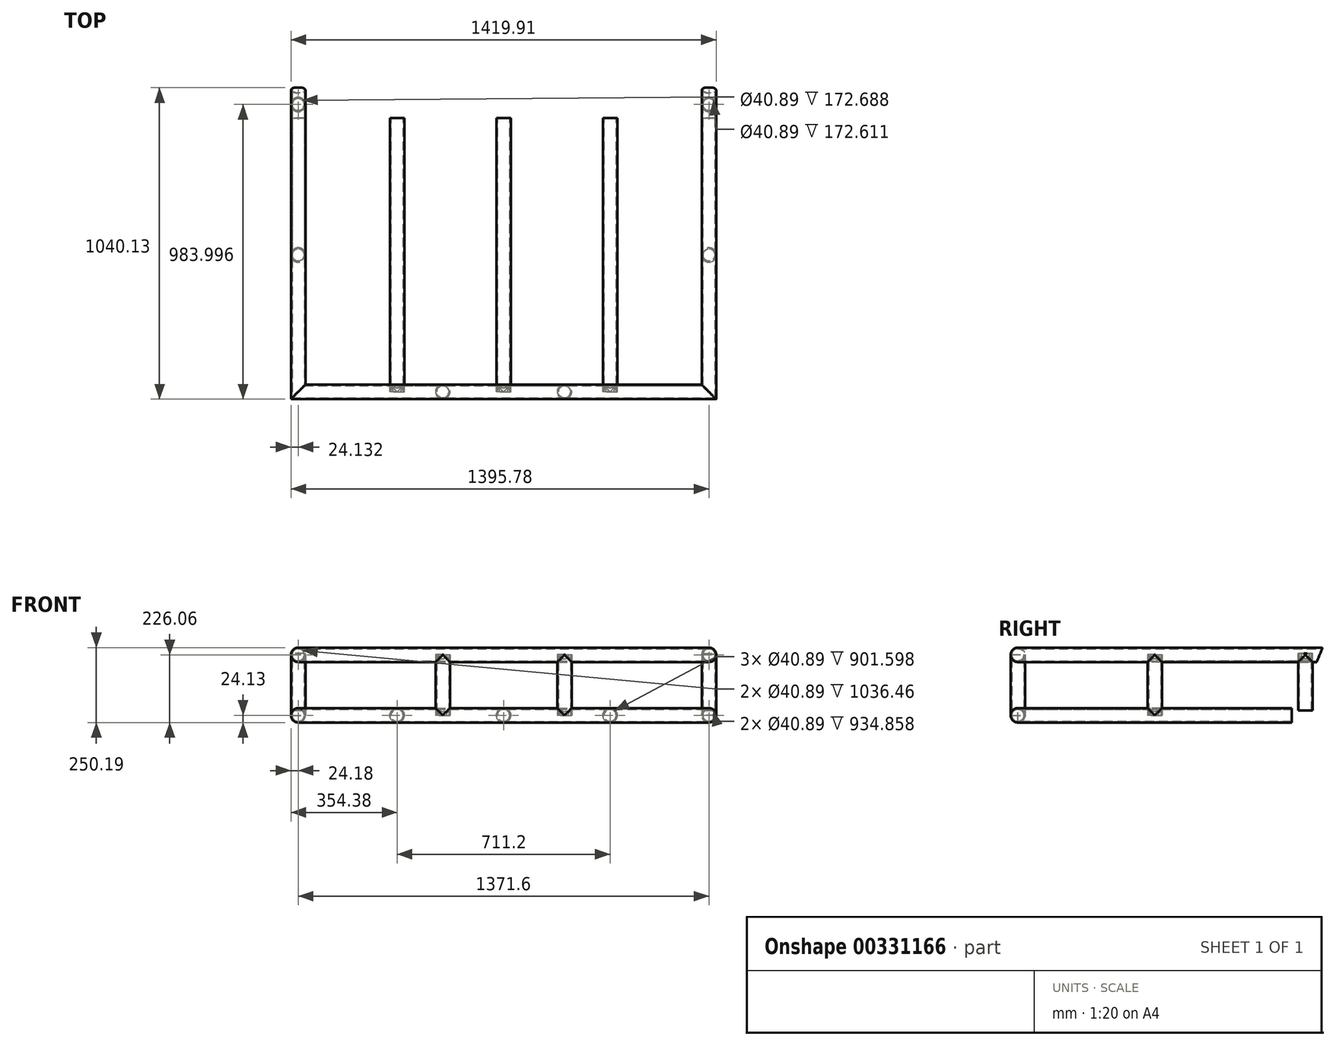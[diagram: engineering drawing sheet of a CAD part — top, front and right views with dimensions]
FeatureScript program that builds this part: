
annotation { "Feature Type Name" : "Feature", "Feature Type Description" : "" }
export const myFeature = defineFeature(function(context is Context, id is Id, definition is map)
    precondition{}
    {
        {
            var Q0;
            Q0=qCreatedBy(makeId("Front.planeOp"),FACE);
            var sketch = newSketch(context, id + "F0", { "sketchPlane" : qUnion([Q0])});
            skCircle(sketch, "E0", {"center": v(-685.8, 0) * mm, "radius": 24.13 * mm});
            skCircle(sketch, "E1", {"center": v(685.8, 0) * mm, "radius": 24.13 * mm});
            skCircle(sketch, "E2", {"center": v(685.8, 0) * mm, "radius": 20.45 * mm});
            skCircle(sketch, "E3", {"center": v(-685.8, 0) * mm, "radius": 20.45 * mm});
            skSolve(sketch);
        }
        {
            var Q0;
            Q0=qCreatedBy(makeId("Top.planeOp"),FACE);
            var sketch = newSketch(context, id + "F1", { "sketchPlane" : qUnion([Q0])});
            skLineSegment(sketch, "E4", {"start": v(-685.8, 0) * mm, "end": v(-685.8, -1016) * mm});
            skLineSegment(sketch, "E5", {"start": v(685.8, 0) * mm, "end": v(685.8, -1016) * mm});
            skLineSegment(sketch, "E6", {"start": v(-685.8, -1016) * mm, "end": v(685.8, -1016) * mm});
            skPoint(sketch, "E7.visualSharp", {"position": v(-685.8, -1016) * mm});
            skLineSegment(sketch, "E7.filletArc", {"start": v(-685.8, -1016) * mm, "end": v(-685.8, -1016) * mm});
            skPoint(sketch, "E8.visualSharp", {"position": v(685.8, -1016) * mm});
            skLineSegment(sketch, "E8.filletArc", {"start": v(685.8, -1016) * mm, "end": v(685.8, -1016) * mm});
            skLineSegment(sketch, "E9", {"start": v(-355.6, -1016) * mm, "end": v(-355.6, 0) * mm});
            skLineSegment(sketch, "E10", {"start": v(355.6, -1016) * mm, "end": v(355.6, 0) * mm});
            skLineSegment(sketch, "E11", {"start": v(0, -1016) * mm, "end": v(0, 0) * mm});
            skPoint(sketch, "E12", {"position": v(-685.8, -914.4) * mm});
            skPoint(sketch, "E13", {"position": v(685.8, -914.4) * mm});
            skPoint(sketch, "E14", {"position": v(-685.8, 0) * mm});
            skPoint(sketch, "E15", {"position": v(685.8, 0) * mm});
            skPoint(sketch, "E16", {"position": v(-355.6, -1016) * mm});
            skPoint(sketch, "E17", {"position": v(355.6, -1016) * mm});
            skSolve(sketch);
        }
        {
            var Q0;
            Q0=qCreatedBy(makeId("Front.planeOp"),FACE);
            var sketch = newSketch(context, id + "F2", { "sketchPlane" : qUnion([Q0])});
            skCircle(sketch, "E18", {"center": v(-355.6, 0) * mm, "radius": 24.13 * mm});
            skCircle(sketch, "E19", {"center": v(0, 0) * mm, "radius": 24.13 * mm});
            skCircle(sketch, "E20", {"center": v(355.6, 0) * mm, "radius": 24.13 * mm});
            skCircle(sketch, "E21", {"center": v(355.6, 0) * mm, "radius": 20.45 * mm});
            skCircle(sketch, "E22", {"center": v(0, 0) * mm, "radius": 20.45 * mm});
            skCircle(sketch, "E23", {"center": v(-355.6, 0) * mm, "radius": 20.45 * mm});
            skSolve(sketch);
        }
        {
            var Q0;
            Q0=makeQuery(id+"F0.imprint","IMPRINT",FACE,{"disambiguationData":[TD([[makeQuery(id+"F0.imprint","IMPRINT",EDGE,{"derivedFrom":sQuery(id+"F0.wireOp",EDGE,"E0")}),1.0]])]});
            var Q1;
            Q1=sQuery(id+"F1.wireOp",EDGE,"E4");
            var Q2;
            Q2=sQuery(id+"F1.wireOp",EDGE,"E7.filletArc");
            var Q3;
            Q3=sQuery(id+"F1.wireOp",EDGE,"E6");
            var Q4;
            Q4=sQuery(id+"F1.wireOp",EDGE,"E8.filletArc");
            var Q5;
            Q5=sQuery(id+"F1.wireOp",EDGE,"E5");
            sweep(context, id + "F3", {"profiles" : qUnion([Q0]), "path" : qUnion([Q1, Q2, Q3, Q4, Q5])});
        }
        {
            var Q0;
            Q0=makeQuery(id+"F2.imprint","IMPRINT",FACE,{"disambiguationData":[TD([[makeQuery(id+"F2.imprint","IMPRINT",EDGE,{"derivedFrom":sQuery(id+"F2.wireOp",EDGE,"E18")}),1.0]])]});
            var Q1;
            Q1=makeQuery(id+"F2.imprint","IMPRINT",FACE,{"disambiguationData":[TD([[makeQuery(id+"F2.imprint","IMPRINT",EDGE,{"derivedFrom":sQuery(id+"F2.wireOp",EDGE,"E19")}),1.0]])]});
            var Q2;
            Q2=makeQuery(id+"F2.imprint","IMPRINT",FACE,{"disambiguationData":[TD([[makeQuery(id+"F2.imprint","IMPRINT",EDGE,{"derivedFrom":sQuery(id+"F2.wireOp",EDGE,"E20")}),1.0]])]});
            extrude(context, id + "F4", {"entities" : qUnion([Q0, Q1, Q2]), "operationType" : NewBodyOperationType.ADD, "depth" : 1016 * mm});
        }
        {
            var Q0;
            Q0=qCreatedBy(makeId("Top.planeOp"),FACE);
            var sketch = newSketch(context, id + "F5", { "sketchPlane" : qUnion([Q0])});
            skCircle(sketch, "E24", {"center": v(-685.8, -558.8) * mm, "radius": 24.13 * mm});
            skCircle(sketch, "E25", {"center": v(685.8, -558.8) * mm, "radius": 24.13 * mm});
            skCircle(sketch, "E26", {"center": v(-203.2, -1016) * mm, "radius": 24.13 * mm});
            skCircle(sketch, "E27", {"center": v(203.2, -1016) * mm, "radius": 24.13 * mm});
            skCircle(sketch, "E28", {"center": v(-685.8, -558.8) * mm, "radius": 20.45 * mm});
            skCircle(sketch, "E29", {"center": v(685.8, -558.8) * mm, "radius": 20.45 * mm});
            skCircle(sketch, "E30", {"center": v(-203.2, -1016) * mm, "radius": 20.45 * mm});
            skCircle(sketch, "E31", {"center": v(203.2, -1016) * mm, "radius": 20.45 * mm});
            skSolve(sketch);
        }
        {
            var Q0;
            Q0 = qSketchRegion(id + "F5", true);
            extrude(context, id + "F6", {"entities" : qUnion([Q0]), "operationType" : NewBodyOperationType.ADD, "depth" : 203.2 * mm});
        }
        {
            var Q0;
            Q0=qCreatedBy(makeId("Front.planeOp"),FACE);
            var sketch = newSketch(context, id + "F7", { "sketchPlane" : qUnion([Q0])});
            skCircle(sketch, "E32", {"center": v(685.8, 201.93) * mm, "radius": 24.13 * mm});
            skCircle(sketch, "E33", {"center": v(-685.8, 201.93) * mm, "radius": 24.13 * mm});
            skCircle(sketch, "E34", {"center": v(685.8, 201.93) * mm, "radius": 20.45 * mm});
            skCircle(sketch, "E35", {"center": v(-685.8, 201.93) * mm, "radius": 20.45 * mm});
            skSolve(sketch);
        }
        {
            var Q0;
            Q0=makeQuery(id+"F7.imprint","IMPRINT",FACE,{"disambiguationData":[TD([[makeQuery(id+"F7.imprint","IMPRINT",EDGE,{"derivedFrom":sQuery(id+"F7.wireOp",EDGE,"E33")}),1.0]])]});
            var sketch = newSketch(context, id + "F8", { "sketchPlane" : qUnion([Q0])});
            skLineSegment(sketch, "E36", {"start": v(-705.18, 207.01) * mm, "end": v(-666.45, 207.01) * mm});
            skSolve(sketch);
        }
        {
            var Q0;
            Q0=makeQuery(id+"F7.imprint","IMPRINT",FACE,{"disambiguationData":[TD([[makeQuery(id+"F7.imprint","IMPRINT",EDGE,{"derivedFrom":sQuery(id+"F7.wireOp",EDGE,"E32")}),1.0]])]});
            var sketch = newSketch(context, id + "F9", { "sketchPlane" : qUnion([Q0])});
            skLineSegment(sketch, "E37", {"start": v(666.42, 197.6) * mm, "end": v(705.03, 196.1) * mm});
            skSolve(sketch);
        }
        {
            var Q0;
            Q0=sQuery(id+"F8.wireOp",EDGE,"E36");
            cPlane(context, id + "F10", {"entities" : qUnion([Q0]), "cplaneType" : CPlaneType.LINE_ANGLE, "offset" : 25.4 * mm, "angle" : 90 * degree, "width" : 152.4 * mm, "height" : 152.4 * mm});
        }
        {
            var Q0;
            Q0=qCreatedBy(id+"F10.planeOp",FACE);
            var sketch = newSketch(context, id + "F11", { "sketchPlane" : qUnion([Q0])});
            skLineSegment(sketch, "E38", {"start": v(-685.8, 0) * mm, "end": v(-685.8, -1016) * mm});
            skLineSegment(sketch, "E39", {"start": v(-685.8, -1016) * mm, "end": v(685.8, -1016) * mm});
            skLineSegment(sketch, "E40", {"start": v(685.8, -1016) * mm, "end": v(685.8, 0) * mm});
            skPoint(sketch, "E41.visualSharp", {"position": v(-685.8, -1016) * mm});
            skLineSegment(sketch, "E41.filletArc", {"start": v(-685.8, -1016) * mm, "end": v(-685.8, -1016) * mm});
            skPoint(sketch, "E42.visualSharp", {"position": v(685.8, -1016) * mm});
            skLineSegment(sketch, "E42.filletArc", {"start": v(685.8, -1016) * mm, "end": v(685.8, -1016) * mm});
            skSolve(sketch);
        }
        {
            var Q0;
            Q0=makeQuery(id+"F7.imprint","IMPRINT",FACE,{"disambiguationData":[TD([[makeQuery(id+"F7.imprint","IMPRINT",EDGE,{"derivedFrom":sQuery(id+"F7.wireOp",EDGE,"E33")}),1.0]])]});
            var Q1;
            Q1=sQuery(id+"F11.wireOp",EDGE,"E38");
            var Q2;
            Q2=sQuery(id+"F11.wireOp",EDGE,"E41.filletArc");
            var Q3;
            Q3=sQuery(id+"F11.wireOp",EDGE,"E39");
            var Q4;
            Q4=sQuery(id+"F11.wireOp",EDGE,"E42.filletArc");
            var Q5;
            Q5=sQuery(id+"F11.wireOp",EDGE,"E40");
            sweep(context, id + "F12", {"operationType" : NewBodyOperationType.ADD, "profiles" : qUnion([Q0]), "path" : qUnion([Q1, Q2, Q3, Q4, Q5])});
        }
        {
            var Q0;
            Q0=qCreatedBy(makeId("Right.planeOp"),FACE);
            var sketch = newSketch(context, id + "F13", { "sketchPlane" : qUnion([Q0])});
            skLineSegment(sketch, "E43.top", {"start": v(0.15, 177.8) * mm, "end": v(-18.03, 177.8) * mm});
            skLineSegment(sketch, "E43.left", {"start": v(0.15, 222.25) * mm, "end": v(0.15, 177.8) * mm});
            skLineSegment(sketch, "E44", {"start": v(0.15, 222.25) * mm, "end": v(-18.03, 177.8) * mm});
            skSolve(sketch);
        }
        {
            var Q0;
            Q0 = qSketchRegion(id + "F13", true);
            extrude(context, id + "F14", {"entities" : qUnion([Q0]), "operationType" : NewBodyOperationType.REMOVE, "endBound" : BoundingType.THROUGH_ALL, "oppositeDirection" : true, "depth" : 25.4 * mm, "hasSecondDirection" : true, "secondDirectionBound" : SecondDirectionBoundingType.THROUGH_ALL, "secondDirectionOppositeDirection" : false, "secondDirectionDepth" : 25.4 * mm});
        }
        {
            var Q0;
            Q0=qCreatedBy(makeId("Right.planeOp"),FACE);
            var sketch = newSketch(context, id + "F15", { "sketchPlane" : qUnion([Q0])});
            skLineSegment(sketch, "E45.bottom", {"start": v(-101.6, 47.84) * mm, "end": v(101.6, 47.84) * mm});
            skLineSegment(sketch, "E45.top", {"start": v(-101.6, -47.84) * mm, "end": v(101.6, -47.84) * mm});
            skLineSegment(sketch, "E45.left", {"start": v(-101.6, 47.84) * mm, "end": v(-101.6, -47.84) * mm});
            skLineSegment(sketch, "E45.right", {"start": v(101.6, 47.84) * mm, "end": v(101.6, -47.84) * mm});
            skPoint(sketch, "E45.middle", {"position": v(0, 0) * mm});
            skSolve(sketch);
        }
        {
            var Q0;
            Q0 = qSketchRegion(id + "F15", true);
            extrude(context, id + "F16", {"entities" : qUnion([Q0]), "operationType" : NewBodyOperationType.REMOVE, "endBound" : BoundingType.THROUGH_ALL, "oppositeDirection" : true, "depth" : 25.4 * mm, "hasSecondDirection" : true, "secondDirectionBound" : SecondDirectionBoundingType.THROUGH_ALL, "secondDirectionOppositeDirection" : false, "secondDirectionDepth" : 25.4 * mm});
        }
        {
            var Q0;
            Q0=qCreatedBy(id+"F10.planeOp",FACE);
            var sketch = newSketch(context, id + "F17", { "sketchPlane" : qUnion([Q0])});
            skCircle(sketch, "E46", {"center": v(-685.85, -56.13) * mm, "radius": 24.13 * mm});
            skCircle(sketch, "E47", {"center": v(685.8, -56.13) * mm, "radius": 24.13 * mm});
            skCircle(sketch, "E48", {"center": v(-685.85, -56.13) * mm, "radius": 20.45 * mm});
            skCircle(sketch, "E49", {"center": v(685.8, -56.13) * mm, "radius": 20.45 * mm});
            skSolve(sketch);
        }
        {
            var Q0;
            Q0 = qSketchRegion(id + "F17", true);
            extrude(context, id + "F18", {"entities" : qUnion([Q0]), "operationType" : NewBodyOperationType.ADD, "oppositeDirection" : true, "depth" : 190.5 * mm});
        }
    });
